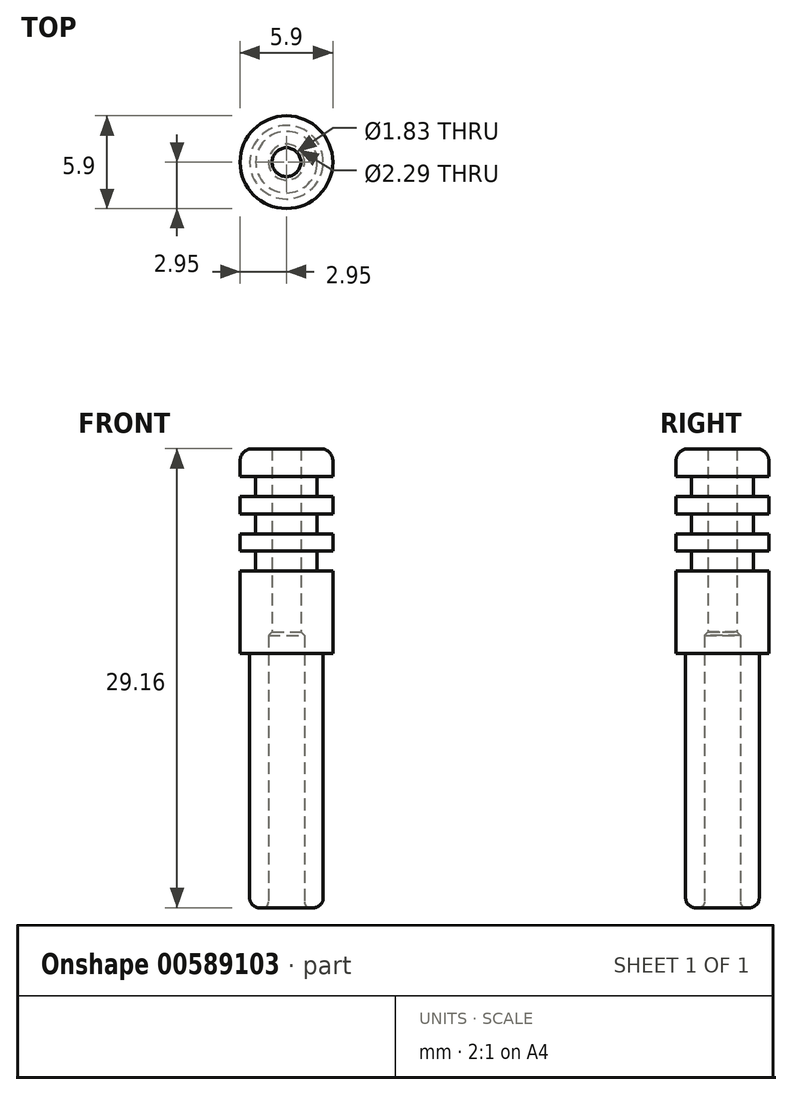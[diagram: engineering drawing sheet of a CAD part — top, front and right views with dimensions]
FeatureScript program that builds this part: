
annotation { "Feature Type Name" : "Feature", "Feature Type Description" : "" }
export const myFeature = defineFeature(function(context is Context, id is Id, definition is map)
    precondition{}
    {
        {
            var Q0;
            Q0=qCreatedBy(makeId("Front.planeOp"),FACE);
            var sketch = newSketch(context, id + "F0", { "sketchPlane" : qUnion([Q0])});
            skLineSegment(sketch, "E0", {"start": v(0.91, 1.37) * mm, "end": v(0.91, 13) * mm});
            skLineSegment(sketch, "E1", {"start": v(0.91, 13) * mm, "end": v(2.18, 13) * mm});
            skLineSegment(sketch, "E2", {"start": v(2.95, 12.24) * mm, "end": v(2.95, 11.25) * mm});
            skLineSegment(sketch, "E3", {"start": v(2.95, 11.25) * mm, "end": v(1.96, 11.25) * mm});
            skLineSegment(sketch, "E4", {"start": v(1.96, 11.25) * mm, "end": v(1.96, 9.98) * mm});
            skLineSegment(sketch, "E5", {"start": v(1.96, 9.98) * mm, "end": v(2.95, 9.98) * mm});
            skLineSegment(sketch, "E6", {"start": v(2.95, 9.98) * mm, "end": v(2.95, 8.86) * mm});
            skLineSegment(sketch, "E7", {"start": v(2.95, 8.87) * mm, "end": v(1.96, 8.87) * mm});
            skLineSegment(sketch, "E8", {"start": v(1.96, 8.87) * mm, "end": v(1.96, 7.6) * mm});
            skLineSegment(sketch, "E9", {"start": v(1.96, 7.6) * mm, "end": v(2.95, 7.6) * mm});
            skLineSegment(sketch, "E10", {"start": v(2.95, 7.6) * mm, "end": v(2.95, 6.5) * mm});
            skLineSegment(sketch, "E11", {"start": v(2.95, 6.5) * mm, "end": v(1.96, 6.5) * mm});
            skLineSegment(sketch, "E12", {"start": v(1.96, 6.5) * mm, "end": v(1.96, 5.23) * mm});
            skLineSegment(sketch, "E13", {"start": v(2.34, 0) * mm, "end": v(2.34, -15.52) * mm});
            skLineSegment(sketch, "E14", {"start": v(1.7, -16.15) * mm, "end": v(1.52, -16.15) * mm});
            skLineSegment(sketch, "E15", {"start": v(1.14, -15.77) * mm, "end": v(1.14, 1.14) * mm});
            skLineSegment(sketch, "E16", {"start": v(1.14, 1.14) * mm, "end": v(0.91, 1.37) * mm});
            skPoint(sketch, "E17.visualSharp", {"position": v(2.95, 13) * mm});
            skArc(sketch, "E17.filletArc", {"start": v(2.95, 12.24) * mm, "mid": v(2.72, 12.78) * mm, "end": v(2.18, 13) * mm});
            skLineSegment(sketch, "E18", {"start": v(1.96, 5.23) * mm, "end": v(2.95, 5.23) * mm});
            skLineSegment(sketch, "E19", {"start": v(2.95, 5.23) * mm, "end": v(2.95, 0) * mm});
            skLineSegment(sketch, "E20", {"start": v(2.95, 0) * mm, "end": v(2.34, 0) * mm});
            skPoint(sketch, "E21.visualSharp", {"position": v(2.34, -16.15) * mm});
            skArc(sketch, "E21.filletArc", {"start": v(1.7, -16.15) * mm, "mid": v(2.15, -15.97) * mm, "end": v(2.34, -15.52) * mm});
            skPoint(sketch, "E22.visualSharp", {"position": v(1.14, -16.15) * mm});
            skArc(sketch, "E22.filletArc", {"start": v(1.14, -15.77) * mm, "mid": v(1.25, -16.04) * mm, "end": v(1.52, -16.15) * mm});
            skLineSegment(sketch, "E23", {"start": v(0, 0) * mm, "end": v(0, 22.51) * mm, "construction": true});
            skSolve(sketch);
        }
        {
            var Q0;
            Q0=qSketchRegion(id+"F0",true);
            var Q1;
            Q1=sQuery(id+"F0.wireOp",EDGE,"E23");
            revolve(context, id + "F1", {"entities" : qUnion([Q0]), "axis" : qUnion([Q1]), "revolveType" : RevolveType.FULL});
        }
    });
